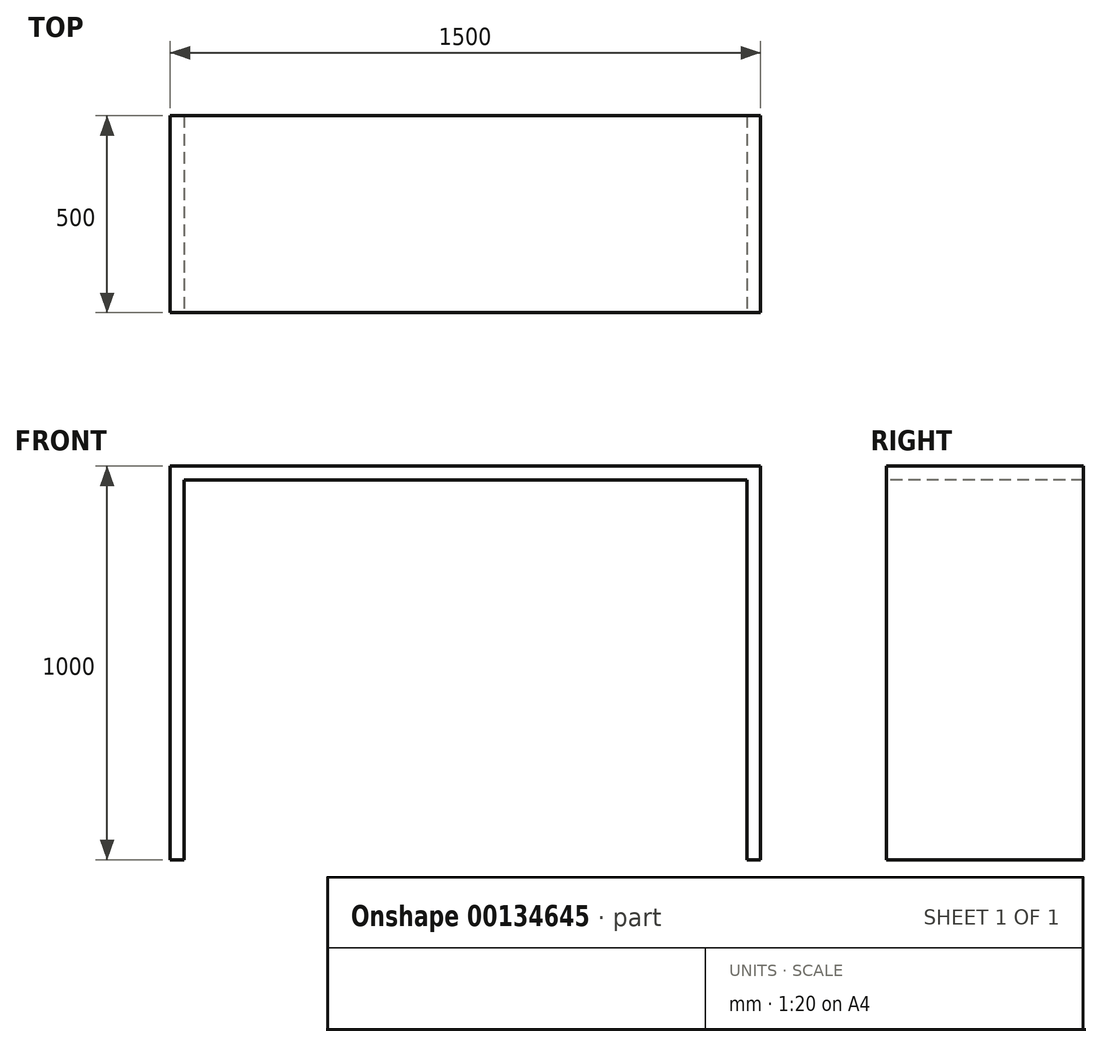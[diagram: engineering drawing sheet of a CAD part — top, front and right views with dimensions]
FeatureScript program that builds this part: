
annotation { "Feature Type Name" : "Feature", "Feature Type Description" : "" }
export const myFeature = defineFeature(function(context is Context, id is Id, definition is map)
    precondition{}
    {
        {
            var Q0;
            Q0=qCreatedBy(makeId("Top.planeOp"),FACE);
            var sketch = newSketch(context, id + "F0", { "sketchPlane" : qUnion([Q0])});
            skLineSegment(sketch, "E0.bottom", {"start": v(750, -250) * mm, "end": v(-750, -250) * mm});
            skLineSegment(sketch, "E0.top", {"start": v(750, 250) * mm, "end": v(-750, 250) * mm});
            skLineSegment(sketch, "E0.left", {"start": v(750, -250) * mm, "end": v(750, 250) * mm});
            skLineSegment(sketch, "E0.right", {"start": v(-750, -250) * mm, "end": v(-750, 250) * mm});
            skPoint(sketch, "E0.middle", {"position": v(0, 0) * mm});
            skSolve(sketch);
        }
        {
            var Q0;
            Q0=makeQuery(id+"F0.imprint","IMPRINT",FACE,{"disambiguationData":[TD([[makeQuery(id+"F0.imprint","IMPRINT",EDGE,{"derivedFrom":sQuery(id+"F0.wireOp",EDGE,"E0.bottom")}),-1.0]])]});
            extrude(context, id + "F1", {"entities" : qUnion([Q0]), "depth" : 1000 * mm});
        }
        {
            var Q0;
            Q0=makeQuery(id+"F1.opExtrude","SWEPT_FACE",FACE,{"disambiguationData":[OSD([sQuery(id+"F0.wireOp",EDGE,"E0.bottom")])]});
            var sketch = newSketch(context, id + "F2", { "sketchPlane" : qUnion([Q0])});
            skLineSegment(sketch, "E1.bottom", {"start": v(-715, 0) * mm, "end": v(715, 0) * mm});
            skLineSegment(sketch, "E1.top", {"start": v(-715, 965) * mm, "end": v(715, 965) * mm});
            skLineSegment(sketch, "E1.left", {"start": v(-715, 0) * mm, "end": v(-715, 965) * mm});
            skLineSegment(sketch, "E1.right", {"start": v(715, 0) * mm, "end": v(715, 965) * mm});
            skSolve(sketch);
        }
        {
            var Q0;
            Q0=makeQuery(id+"F2.imprint","IMPRINT",FACE,{"disambiguationData":[TD([[makeQuery(id+"F2.imprint","IMPRINT",EDGE,{"derivedFrom":sQuery(id+"F2.wireOp",EDGE,"E1.bottom")}),-1.0]])]});
            extrude(context, id + "F3", {"entities" : qUnion([Q0]), "operationType" : NewBodyOperationType.REMOVE, "oppositeDirection" : true, "depth" : 500 * mm});
        }
    });
